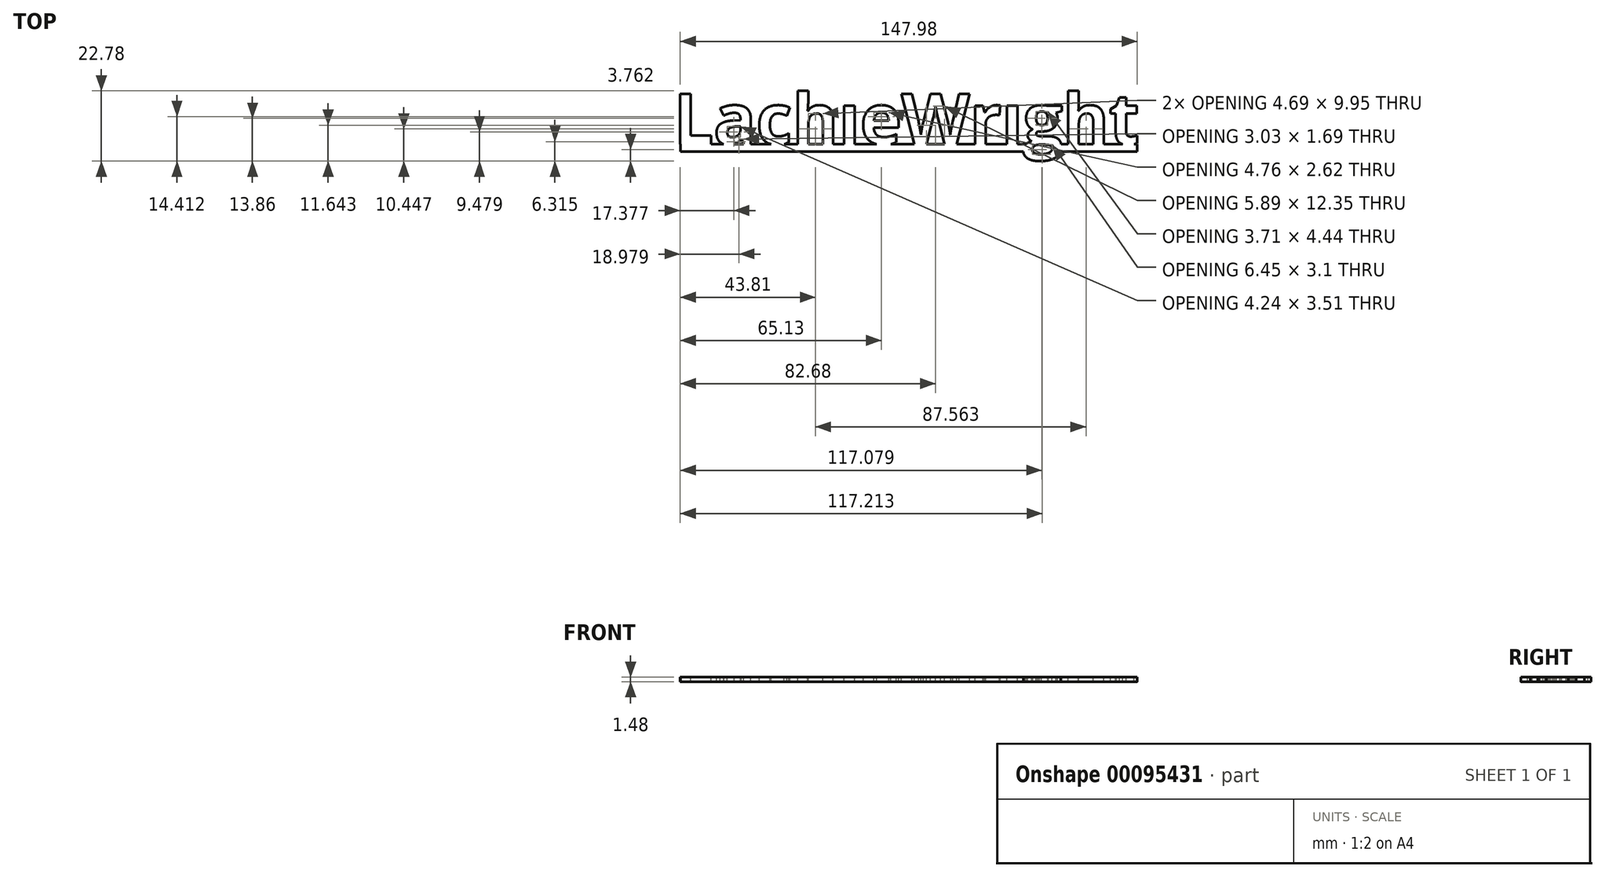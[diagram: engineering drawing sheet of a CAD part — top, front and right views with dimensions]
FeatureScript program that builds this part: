
annotation { "Feature Type Name" : "Feature", "Feature Type Description" : "" }
export const myFeature = defineFeature(function(context is Context, id is Id, definition is map)
    precondition{}
    {
        {
            var Q0;
            Q0=qCreatedBy(makeId("Top.planeOp"),FACE);
            var sketch = newSketch(context, id + "F0", { "sketchPlane" : qUnion([Q0])});
            skText(sketch, "E0", { "text": "LachieWright", "fontName": "OpenSans-Bold.ttf"});
            skLineSegment(sketch, "E1.bottom", {"start": v(2.22, 0) * mm, "end": v(150, 0) * mm});
            skLineSegment(sketch, "E1.top", {"start": v(2.22, -2.33) * mm, "end": v(150, -2.33) * mm});
            skLineSegment(sketch, "E1.left", {"start": v(2.22, 0) * mm, "end": v(2.22, -2.33) * mm});
            skLineSegment(sketch, "E1.right", {"start": v(150, 0) * mm, "end": v(150, -2.33) * mm});
            const initialGuessF0  = {"E0": [0, 0, 1, 0, 0.0164]};
            skSetInitialGuess(sketch, initialGuessF0);
            skSolve(sketch);
        }
        {
            var Q0;
            Q0 = qSketchRegion(id + "F0", true);
            extrude(context, id + "F1", {"entities" : qUnion([Q0]), "oppositeDirection" : true, "depth" : 1.48 * mm});
        }
        {
            var Q0;
            Q0=makeQuery(id+"F1.opExtrude","CAP_FACE",FACE,{"disambiguationData":[OSD([sQuery(id+"F0.wireOp",EDGE,"E0.sketch_text.stroke-0"),sQuery(id+"F0.wireOp",EDGE,"E0.sketch_text.stroke-1"),sQuery(id+"F0.wireOp",EDGE,"E0.sketch_text.stroke-2"),sQuery(id+"F0.wireOp",EDGE,"E0.sketch_text.stroke-3"),sQuery(id+"F0.wireOp",EDGE,"E0.sketch_text.stroke-4"),sQuery(id+"F0.wireOp",EDGE,"E0.sketch_text.stroke-5"),sQuery(id+"F0.wireOp",EDGE,"E0.sketch_text.stroke-6"),sQuery(id+"F0.wireOp",EDGE,"E0.sketch_text.stroke-7"),sQuery(id+"F0.wireOp",EDGE,"E0.sketch_text.stroke-8"),sQuery(id+"F0.wireOp",EDGE,"E0.sketch_text.stroke-9"),sQuery(id+"F0.wireOp",EDGE,"E0.sketch_text.stroke-10"),sQuery(id+"F0.wireOp",EDGE,"E0.sketch_text.stroke-11"),sQuery(id+"F0.wireOp",EDGE,"E0.sketch_text.stroke-12"),sQuery(id+"F0.wireOp",EDGE,"E0.sketch_text.stroke-13"),sQuery(id+"F0.wireOp",EDGE,"E0.sketch_text.stroke-14"),sQuery(id+"F0.wireOp",EDGE,"E0.sketch_text.stroke-15"),sQuery(id+"F0.wireOp",EDGE,"E0.sketch_text.stroke-16"),sQuery(id+"F0.wireOp",EDGE,"E0.sketch_text.stroke-17"),sQuery(id+"F0.wireOp",EDGE,"E0.sketch_text.stroke-18"),sQuery(id+"F0.wireOp",EDGE,"E0.sketch_text.stroke-19"),sQuery(id+"F0.wireOp",EDGE,"E0.sketch_text.stroke-20"),sQuery(id+"F0.wireOp",EDGE,"E0.sketch_text.stroke-21"),sQuery(id+"F0.wireOp",EDGE,"E0.sketch_text.stroke-22"),sQuery(id+"F0.wireOp",EDGE,"E0.sketch_text.stroke-24"),sQuery(id+"F0.wireOp",EDGE,"E0.sketch_text.stroke-25"),sQuery(id+"F0.wireOp",EDGE,"E0.sketch_text.stroke-26"),sQuery(id+"F0.wireOp",EDGE,"E0.sketch_text.stroke-27"),sQuery(id+"F0.wireOp",EDGE,"E0.sketch_text.stroke-28"),sQuery(id+"F0.wireOp",EDGE,"E0.sketch_text.stroke-29"),sQuery(id+"F0.wireOp",EDGE,"E0.sketch_text.stroke-30"),sQuery(id+"F0.wireOp",EDGE,"E0.sketch_text.stroke-31"),sQuery(id+"F0.wireOp",EDGE,"E0.sketch_text.stroke-32"),sQuery(id+"F0.wireOp",EDGE,"E0.sketch_text.stroke-33"),sQuery(id+"F0.wireOp",EDGE,"E0.sketch_text.stroke-34"),sQuery(id+"F0.wireOp",EDGE,"E0.sketch_text.stroke-35"),sQuery(id+"F0.wireOp",EDGE,"E0.sketch_text.stroke-36"),sQuery(id+"F0.wireOp",EDGE,"E0.sketch_text.stroke-37"),sQuery(id+"F0.wireOp",EDGE,"E0.sketch_text.stroke-38"),sQuery(id+"F0.wireOp",EDGE,"E0.sketch_text.stroke-39"),sQuery(id+"F0.wireOp",EDGE,"E0.sketch_text.stroke-40"),sQuery(id+"F0.wireOp",EDGE,"E0.sketch_text.stroke-41"),sQuery(id+"F0.wireOp",EDGE,"E0.sketch_text.stroke-42"),sQuery(id+"F0.wireOp",EDGE,"E0.sketch_text.stroke-43"),sQuery(id+"F0.wireOp",EDGE,"E0.sketch_text.stroke-46"),sQuery(id+"F0.wireOp",EDGE,"E0.sketch_text.stroke-47"),sQuery(id+"F0.wireOp",EDGE,"E0.sketch_text.stroke-48"),sQuery(id+"F0.wireOp",EDGE,"E0.sketch_text.stroke-49"),sQuery(id+"F0.wireOp",EDGE,"E0.sketch_text.stroke-50"),sQuery(id+"F0.wireOp",EDGE,"E0.sketch_text.stroke-52"),sQuery(id+"F0.wireOp",EDGE,"E0.sketch_text.stroke-53"),sQuery(id+"F0.wireOp",EDGE,"E0.sketch_text.stroke-54"),sQuery(id+"F0.wireOp",EDGE,"E0.sketch_text.stroke-55"),sQuery(id+"F0.wireOp",EDGE,"E0.sketch_text.stroke-56"),sQuery(id+"F0.wireOp",EDGE,"E0.sketch_text.stroke-57"),sQuery(id+"F0.wireOp",EDGE,"E0.sketch_text.stroke-58"),sQuery(id+"F0.wireOp",EDGE,"E0.sketch_text.stroke-59"),sQuery(id+"F0.wireOp",EDGE,"E0.sketch_text.stroke-60"),sQuery(id+"F0.wireOp",EDGE,"E0.sketch_text.stroke-61"),sQuery(id+"F0.wireOp",EDGE,"E0.sketch_text.stroke-68"),sQuery(id+"F0.wireOp",EDGE,"E0.sketch_text.stroke-69"),sQuery(id+"F0.wireOp",EDGE,"E0.sketch_text.stroke-70"),sQuery(id+"F0.wireOp",EDGE,"E0.sketch_text.stroke-71"),sQuery(id+"F0.wireOp",EDGE,"E0.sketch_text.stroke-72"),sQuery(id+"F0.wireOp",EDGE,"E0.sketch_text.stroke-73"),sQuery(id+"F0.wireOp",EDGE,"E0.sketch_text.stroke-74"),sQuery(id+"F0.wireOp",EDGE,"E0.sketch_text.stroke-75"),sQuery(id+"F0.wireOp",EDGE,"E0.sketch_text.stroke-76"),sQuery(id+"F0.wireOp",EDGE,"E0.sketch_text.stroke-77"),sQuery(id+"F0.wireOp",EDGE,"E0.sketch_text.stroke-78"),sQuery(id+"F0.wireOp",EDGE,"E0.sketch_text.stroke-79"),sQuery(id+"F0.wireOp",EDGE,"E0.sketch_text.stroke-80"),sQuery(id+"F0.wireOp",EDGE,"E0.sketch_text.stroke-81"),sQuery(id+"F0.wireOp",EDGE,"E0.sketch_text.stroke-82"),sQuery(id+"F0.wireOp",EDGE,"E0.sketch_text.stroke-83"),sQuery(id+"F0.wireOp",EDGE,"E0.sketch_text.stroke-84"),sQuery(id+"F0.wireOp",EDGE,"E0.sketch_text.stroke-85"),sQuery(id+"F0.wireOp",EDGE,"E0.sketch_text.stroke-86"),sQuery(id+"F0.wireOp",EDGE,"E0.sketch_text.stroke-87"),sQuery(id+"F0.wireOp",EDGE,"E0.sketch_text.stroke-88"),sQuery(id+"F0.wireOp",EDGE,"E0.sketch_text.stroke-89"),sQuery(id+"F0.wireOp",EDGE,"E0.sketch_text.stroke-92"),sQuery(id+"F0.wireOp",EDGE,"E0.sketch_text.stroke-93"),sQuery(id+"F0.wireOp",EDGE,"E0.sketch_text.stroke-94"),sQuery(id+"F0.wireOp",EDGE,"E0.sketch_text.stroke-95"),sQuery(id+"F0.wireOp",EDGE,"E0.sketch_text.stroke-96"),sQuery(id+"F0.wireOp",EDGE,"E0.sketch_text.stroke-97"),sQuery(id+"F0.wireOp",EDGE,"E0.sketch_text.stroke-99"),sQuery(id+"F0.wireOp",EDGE,"E0.sketch_text.stroke-100"),sQuery(id+"F0.wireOp",EDGE,"E0.sketch_text.stroke-101"),sQuery(id+"F0.wireOp",EDGE,"E0.sketch_text.stroke-102"),sQuery(id+"F0.wireOp",EDGE,"E0.sketch_text.stroke-103"),sQuery(id+"F0.wireOp",EDGE,"E0.sketch_text.stroke-104"),sQuery(id+"F0.wireOp",EDGE,"E0.sketch_text.stroke-105"),sQuery(id+"F0.wireOp",EDGE,"E0.sketch_text.stroke-106"),sQuery(id+"F0.wireOp",EDGE,"E0.sketch_text.stroke-107"),sQuery(id+"F0.wireOp",EDGE,"E0.sketch_text.stroke-108"),sQuery(id+"F0.wireOp",EDGE,"E0.sketch_text.stroke-109"),sQuery(id+"F0.wireOp",EDGE,"E0.sketch_text.stroke-110"),sQuery(id+"F0.wireOp",EDGE,"E0.sketch_text.stroke-111"),sQuery(id+"F0.wireOp",EDGE,"E0.sketch_text.stroke-112"),sQuery(id+"F0.wireOp",EDGE,"E0.sketch_text.stroke-113"),sQuery(id+"F0.wireOp",EDGE,"E0.sketch_text.stroke-114"),sQuery(id+"F0.wireOp",EDGE,"E0.sketch_text.stroke-115"),sQuery(id+"F0.wireOp",EDGE,"E0.sketch_text.stroke-116"),sQuery(id+"F0.wireOp",EDGE,"E0.sketch_text.stroke-117"),sQuery(id+"F0.wireOp",EDGE,"E0.sketch_text.stroke-118"),sQuery(id+"F0.wireOp",EDGE,"E0.sketch_text.stroke-119"),sQuery(id+"F0.wireOp",EDGE,"E0.sketch_text.stroke-120"),sQuery(id+"F0.wireOp",EDGE,"E0.sketch_text.stroke-122"),sQuery(id+"F0.wireOp",EDGE,"E0.sketch_text.stroke-123"),sQuery(id+"F0.wireOp",EDGE,"E0.sketch_text.stroke-124"),sQuery(id+"F0.wireOp",EDGE,"E0.sketch_text.stroke-125"),sQuery(id+"F0.wireOp",EDGE,"E0.sketch_text.stroke-126"),sQuery(id+"F0.wireOp",EDGE,"E0.sketch_text.stroke-127"),sQuery(id+"F0.wireOp",EDGE,"E0.sketch_text.stroke-134"),sQuery(id+"F0.wireOp",EDGE,"E0.sketch_text.stroke-135"),sQuery(id+"F0.wireOp",EDGE,"E0.sketch_text.stroke-136"),sQuery(id+"F0.wireOp",EDGE,"E0.sketch_text.stroke-137"),sQuery(id+"F0.wireOp",EDGE,"E0.sketch_text.stroke-138"),sQuery(id+"F0.wireOp",EDGE,"E0.sketch_text.stroke-139"),sQuery(id+"F0.wireOp",EDGE,"E0.sketch_text.stroke-140"),sQuery(id+"F0.wireOp",EDGE,"E0.sketch_text.stroke-141"),sQuery(id+"F0.wireOp",EDGE,"E0.sketch_text.stroke-142"),sQuery(id+"F0.wireOp",EDGE,"E0.sketch_text.stroke-143"),sQuery(id+"F0.wireOp",EDGE,"E0.sketch_text.stroke-144"),sQuery(id+"F0.wireOp",EDGE,"E0.sketch_text.stroke-145"),sQuery(id+"F0.wireOp",EDGE,"E0.sketch_text.stroke-146"),sQuery(id+"F0.wireOp",EDGE,"E0.sketch_text.stroke-147"),sQuery(id+"F0.wireOp",EDGE,"E0.sketch_text.stroke-148"),sQuery(id+"F0.wireOp",EDGE,"E0.sketch_text.stroke-149"),sQuery(id+"F0.wireOp",EDGE,"E0.sketch_text.stroke-150"),sQuery(id+"F0.wireOp",EDGE,"E0.sketch_text.stroke-151"),sQuery(id+"F0.wireOp",EDGE,"E0.sketch_text.stroke-152"),sQuery(id+"F0.wireOp",EDGE,"E0.sketch_text.stroke-154"),sQuery(id+"F0.wireOp",EDGE,"E0.sketch_text.stroke-155"),sQuery(id+"F0.wireOp",EDGE,"E0.sketch_text.stroke-156"),sQuery(id+"F0.wireOp",EDGE,"E0.sketch_text.stroke-157"),sQuery(id+"F0.wireOp",EDGE,"E0.sketch_text.stroke-158"),sQuery(id+"F0.wireOp",EDGE,"E0.sketch_text.stroke-159"),sQuery(id+"F0.wireOp",EDGE,"E0.sketch_text.stroke-160"),sQuery(id+"F0.wireOp",EDGE,"E0.sketch_text.stroke-161"),sQuery(id+"F0.wireOp",EDGE,"E0.sketch_text.stroke-162"),sQuery(id+"F0.wireOp",EDGE,"E0.sketch_text.stroke-163"),sQuery(id+"F0.wireOp",EDGE,"E0.sketch_text.stroke-164"),sQuery(id+"F0.wireOp",EDGE,"E0.sketch_text.stroke-165"),sQuery(id+"F0.wireOp",EDGE,"E0.sketch_text.stroke-166"),sQuery(id+"F0.wireOp",EDGE,"E0.sketch_text.stroke-167"),sQuery(id+"F0.wireOp",EDGE,"E0.sketch_text.stroke-168"),sQuery(id+"F0.wireOp",EDGE,"E0.sketch_text.stroke-169"),sQuery(id+"F0.wireOp",EDGE,"E0.sketch_text.stroke-170"),sQuery(id+"F0.wireOp",EDGE,"E0.sketch_text.stroke-171"),sQuery(id+"F0.wireOp",EDGE,"E0.sketch_text.stroke-172"),sQuery(id+"F0.wireOp",EDGE,"E0.sketch_text.stroke-173"),sQuery(id+"F0.wireOp",EDGE,"E0.sketch_text.stroke-174"),sQuery(id+"F0.wireOp",EDGE,"E0.sketch_text.stroke-175"),sQuery(id+"F0.wireOp",EDGE,"E0.sketch_text.stroke-176"),sQuery(id+"F0.wireOp",EDGE,"E0.sketch_text.stroke-177"),sQuery(id+"F0.wireOp",EDGE,"E0.sketch_text.stroke-178"),sQuery(id+"F0.wireOp",EDGE,"E0.sketch_text.stroke-179"),sQuery(id+"F0.wireOp",EDGE,"E0.sketch_text.stroke-180"),sQuery(id+"F0.wireOp",EDGE,"E0.sketch_text.stroke-182"),sQuery(id+"F0.wireOp",EDGE,"E0.sketch_text.stroke-183"),sQuery(id+"F0.wireOp",EDGE,"E0.sketch_text.stroke-184"),sQuery(id+"F0.wireOp",EDGE,"E0.sketch_text.stroke-185"),sQuery(id+"F0.wireOp",EDGE,"E0.sketch_text.stroke-186"),sQuery(id+"F0.wireOp",EDGE,"E0.sketch_text.stroke-188"),sQuery(id+"F0.wireOp",EDGE,"E0.sketch_text.stroke-189"),sQuery(id+"F0.wireOp",EDGE,"E0.sketch_text.stroke-190"),sQuery(id+"F0.wireOp",EDGE,"E0.sketch_text.stroke-191"),sQuery(id+"F0.wireOp",EDGE,"E0.sketch_text.stroke-192"),sQuery(id+"F0.wireOp",EDGE,"E0.sketch_text.stroke-193"),sQuery(id+"F0.wireOp",EDGE,"E0.sketch_text.stroke-194"),sQuery(id+"F0.wireOp",EDGE,"E0.sketch_text.stroke-195"),sQuery(id+"F0.wireOp",EDGE,"E0.sketch_text.stroke-196"),sQuery(id+"F0.wireOp",EDGE,"E0.sketch_text.stroke-197"),sQuery(id+"F0.wireOp",EDGE,"E0.sketch_text.stroke-198"),sQuery(id+"F0.wireOp",EDGE,"E0.sketch_text.stroke-199"),sQuery(id+"F0.wireOp",EDGE,"E0.sketch_text.stroke-200"),sQuery(id+"F0.wireOp",EDGE,"E0.sketch_text.stroke-201"),sQuery(id+"F0.wireOp",EDGE,"E0.sketch_text.stroke-202"),sQuery(id+"F0.wireOp",EDGE,"E0.sketch_text.stroke-203"),sQuery(id+"F0.wireOp",EDGE,"E0.sketch_text.stroke-204"),sQuery(id+"F0.wireOp",EDGE,"E0.sketch_text.stroke-205"),sQuery(id+"F0.wireOp",EDGE,"E0.sketch_text.stroke-206"),sQuery(id+"F0.wireOp",EDGE,"E0.sketch_text.stroke-207"),sQuery(id+"F0.wireOp",EDGE,"E0.sketch_text.stroke-208"),sQuery(id+"F0.wireOp",EDGE,"E0.sketch_text.stroke-209"),sQuery(id+"F0.wireOp",EDGE,"E0.sketch_text.stroke-210"),sQuery(id+"F0.wireOp",EDGE,"E0.sketch_text.stroke-211"),sQuery(id+"F0.wireOp",EDGE,"E0.sketch_text.stroke-212"),sQuery(id+"F0.wireOp",EDGE,"E0.sketch_text.stroke-213"),sQuery(id+"F0.wireOp",EDGE,"E0.sketch_text.stroke-214"),sQuery(id+"F0.wireOp",EDGE,"E0.sketch_text.stroke-215"),sQuery(id+"F0.wireOp",EDGE,"E1.bottom"),sQuery(id+"F0.wireOp",EDGE,"E1.top"),sQuery(id+"F0.wireOp",EDGE,"E1.left"),sQuery(id+"F0.wireOp",EDGE,"E1.right")])],"isStart":true});
            var sketch = newSketch(context, id + "F2", { "sketchPlane" : qUnion([Q0])});
            skLineSegment(sketch, "E2", {"start": v(47.97, 19) * mm, "end": v(51.91, 13.28) * mm});
            skLineSegment(sketch, "E3", {"start": v(51.91, 13.28) * mm, "end": v(61.24, 13.65) * mm});
            skLineSegment(sketch, "E4", {"start": v(61.24, 13.65) * mm, "end": v(66.18, 20.55) * mm});
            skLineSegment(sketch, "E5", {"start": v(66.18, 20.55) * mm, "end": v(106.1, 15.07) * mm});
            skLineSegment(sketch, "E6", {"start": v(106.1, 15.07) * mm, "end": v(108.3, 13.1) * mm});
            skLineSegment(sketch, "E7", {"start": v(108.3, 13.1) * mm, "end": v(113.53, 14.03) * mm});
            skLineSegment(sketch, "E8", {"start": v(113.53, 14.03) * mm, "end": v(113.11, 25.67) * mm});
            skLineSegment(sketch, "E9", {"start": v(113.11, 25.67) * mm, "end": v(51.66, 26.4) * mm});
            skLineSegment(sketch, "E10", {"start": v(51.66, 26.4) * mm, "end": v(47.97, 19) * mm});
            skSolve(sketch);
        }
        {
            var Q0;
            Q0=makeQuery(id+"F2.imprint","IMPRINT",FACE,{"disambiguationData":[TD([[makeQuery(id+"F2.imprint","IMPRINT",EDGE,{"derivedFrom":sQuery(id+"F2.wireOp",EDGE,"E2")}),1.0]])]});
            extrude(context, id + "F3", {"entities" : qUnion([Q0]), "operationType" : NewBodyOperationType.REMOVE, "oppositeDirection" : true, "depth" : 25 * mm});
        }
    });
